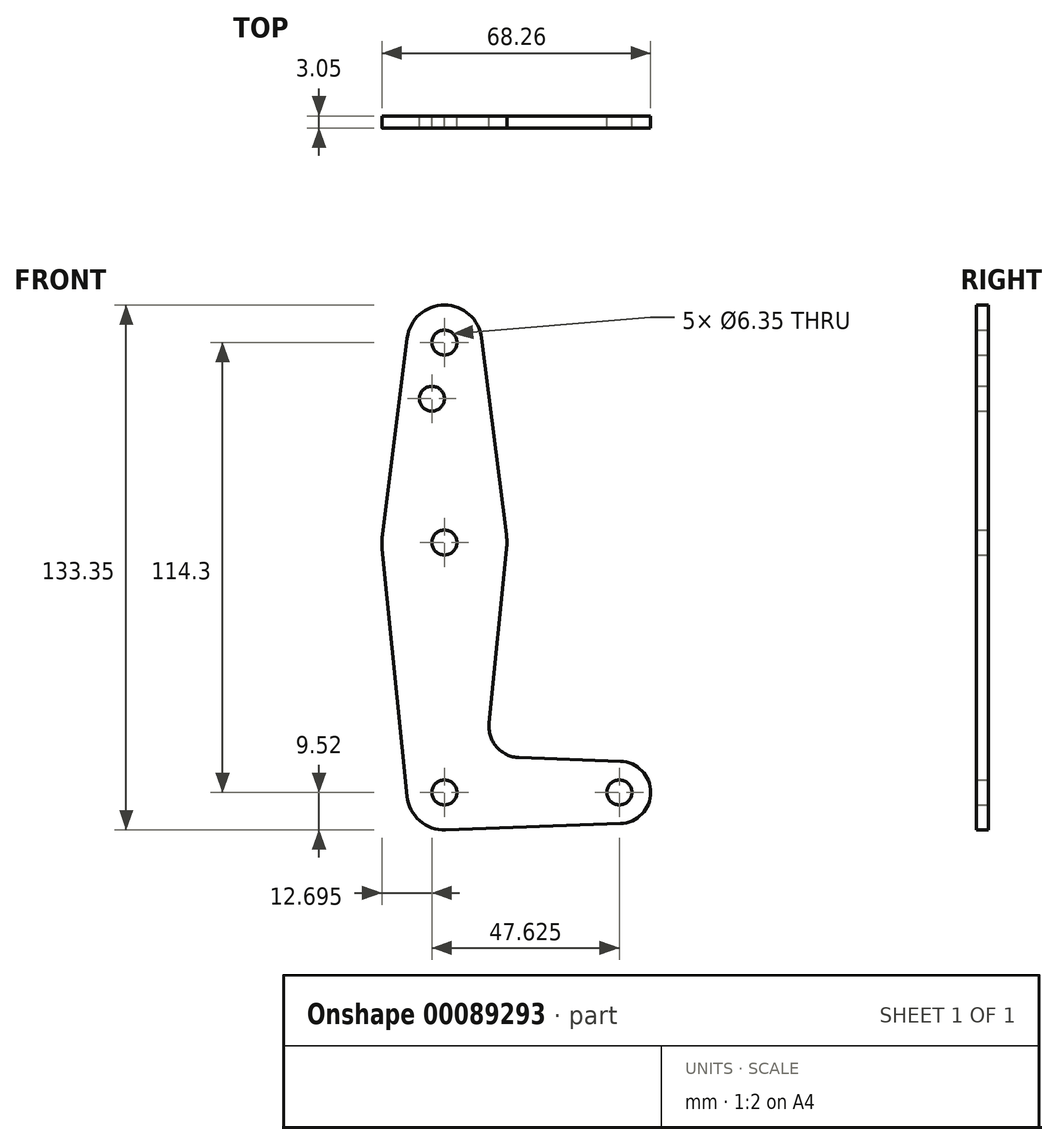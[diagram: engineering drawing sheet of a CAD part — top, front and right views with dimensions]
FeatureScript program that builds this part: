
annotation { "Feature Type Name" : "Feature", "Feature Type Description" : "" }
export const myFeature = defineFeature(function(context is Context, id is Id, definition is map)
    precondition{}
    {
        {
            var Q0;
            Q0=qCreatedBy(makeId("Front.planeOp"),FACE);
            var sketch = newSketch(context, id + "F0", { "sketchPlane" : qUnion([Q0])});
            skLineSegment(sketch, "E0", {"start": v(0, 0) * mm, "end": v(0, 114.3) * mm, "construction": true});
            skLineSegment(sketch, "E1", {"start": v(0, 0) * mm, "end": v(44.45, 0) * mm, "construction": true});
            skCircle(sketch, "E2", {"center": v(0, 114.3) * mm, "radius": 9.52 * mm});
            skCircle(sketch, "E3", {"center": v(0, 63.5) * mm, "radius": 15.88 * mm});
            skCircle(sketch, "E4", {"center": v(0, 0) * mm, "radius": 9.53 * mm});
            skCircle(sketch, "E5", {"center": v(44.45, 0) * mm, "radius": 7.94 * mm});
            skLineSegment(sketch, "E6", {"start": v(-9.45, 115.5) * mm, "end": v(-15.75, 65.48) * mm});
            skLineSegment(sketch, "E7", {"start": v(9.45, 115.5) * mm, "end": v(15.75, 65.48) * mm});
            skLineSegment(sketch, "E8", {"start": v(15.8, 61.91) * mm, "end": v(11.34, 17.6) * mm});
            skLineSegment(sketch, "E9", {"start": v(-15.8, 61.91) * mm, "end": v(-9.48, -0.95) * mm});
            skLineSegment(sketch, "E10", {"start": v(18.97, 8.85) * mm, "end": v(44.73, 7.93) * mm});
            skLineSegment(sketch, "E11", {"start": v(0.34, -9.52) * mm, "end": v(44.73, -7.93) * mm});
            skCircle(sketch, "E12", {"center": v(0, 114.3) * mm, "radius": 3.18 * mm});
            skCircle(sketch, "E13", {"center": v(0, 63.5) * mm, "radius": 3.18 * mm});
            skCircle(sketch, "E14", {"center": v(0, 0) * mm, "radius": 3.18 * mm});
            skCircle(sketch, "E15", {"center": v(44.45, 0) * mm, "radius": 3.18 * mm});
            skCircle(sketch, "E16", {"center": v(-3.18, 100.03) * mm, "radius": 3.18 * mm});
            skArc(sketch, "E17.filletArc", {"start": v(11.34, 17.6) * mm, "mid": v(13.26, 11.57) * mm, "end": v(18.97, 8.85) * mm});
            skSolve(sketch);
        }
        {
            var Q0;
            Q0 = qSketchRegion(id + "F0", true);
            extrude(context, id + "F1", {"entities" : qUnion([Q0]), "depth" : 3.05 * mm});
        }
    });
